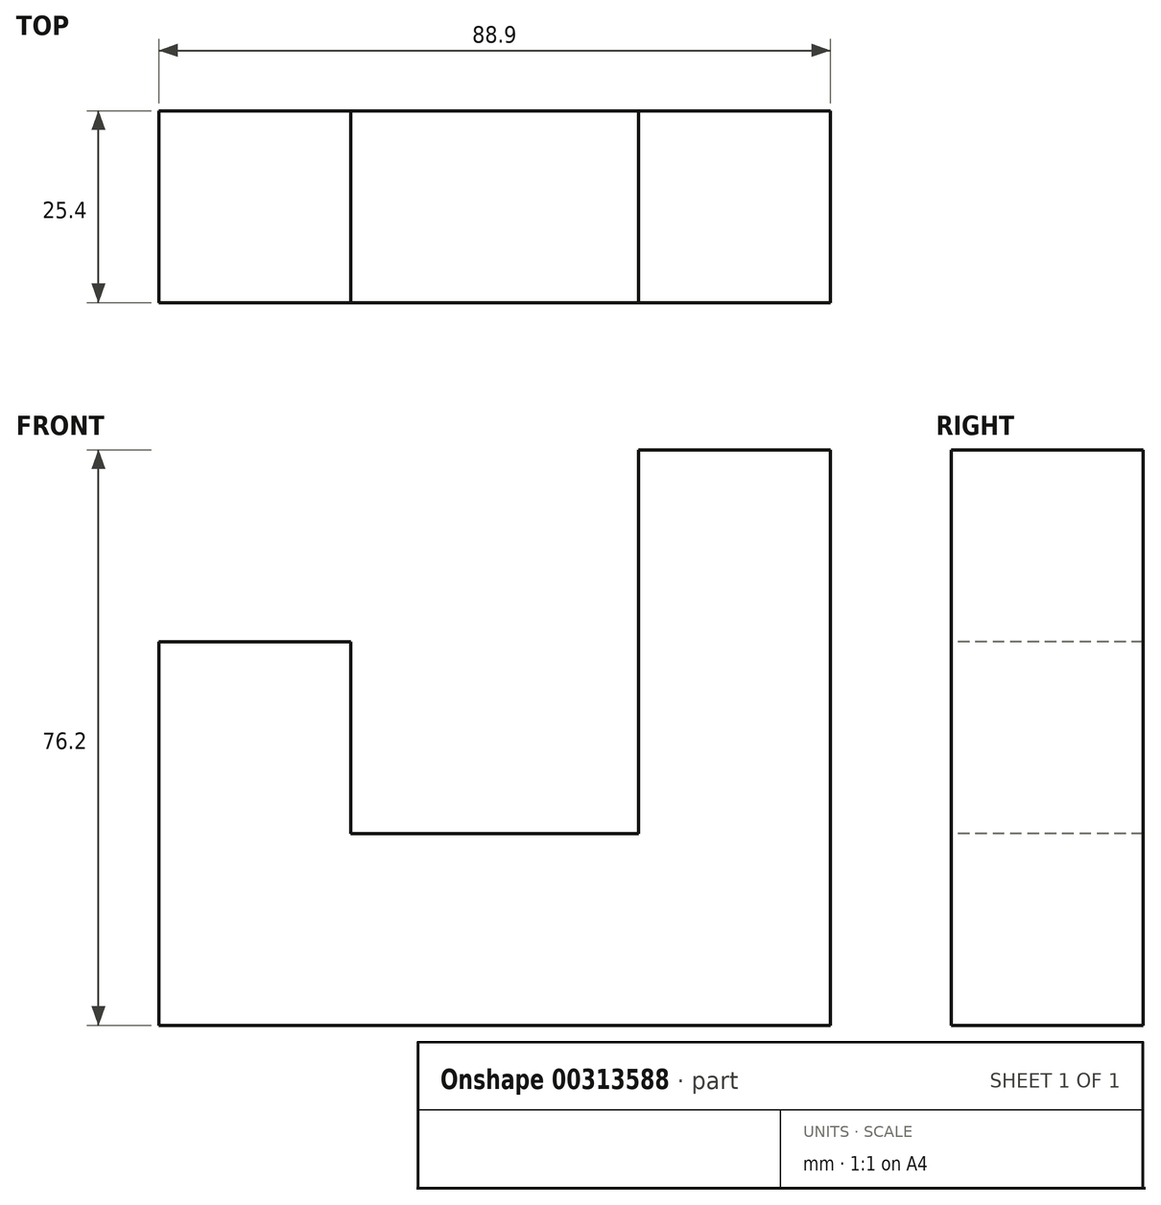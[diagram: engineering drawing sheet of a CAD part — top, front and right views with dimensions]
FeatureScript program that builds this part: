
annotation { "Feature Type Name" : "Feature", "Feature Type Description" : "" }
export const myFeature = defineFeature(function(context is Context, id is Id, definition is map)
    precondition{}
    {
        {
            var Q0;
            Q0=qCreatedBy(makeId("Front.planeOp"),FACE);
            var sketch = newSketch(context, id + "F0", { "sketchPlane" : qUnion([Q0])});
            skLineSegment(sketch, "E0", {"start": v(-38.56, -63.93) * mm, "end": v(50.34, -63.93) * mm});
            skLineSegment(sketch, "E1", {"start": v(50.34, -63.93) * mm, "end": v(50.34, 12.27) * mm});
            skLineSegment(sketch, "E2", {"start": v(50.34, 12.27) * mm, "end": v(24.94, 12.27) * mm});
            skLineSegment(sketch, "E3", {"start": v(24.94, 12.27) * mm, "end": v(24.94, -38.53) * mm});
            skLineSegment(sketch, "E4", {"start": v(24.94, -38.53) * mm, "end": v(-13.16, -38.53) * mm});
            skLineSegment(sketch, "E5", {"start": v(-13.16, -38.53) * mm, "end": v(-13.16, -13.13) * mm});
            skLineSegment(sketch, "E6", {"start": v(-13.16, -13.13) * mm, "end": v(-38.56, -13.13) * mm});
            skLineSegment(sketch, "E7", {"start": v(-38.56, -13.13) * mm, "end": v(-38.56, -63.93) * mm});
            skLineSegment(sketch, "E8", {"start": v(-38.56, -63.93) * mm, "end": v(-38.56, -63.93) * mm});
            skSolve(sketch);
        }
        {
            var Q0;
            Q0 = qSketchRegion(id + "F0", true);
            extrude(context, id + "F1", {"entities" : qUnion([Q0]), "oppositeDirection" : true, "depth" : 25.4 * mm});
        }
    });
